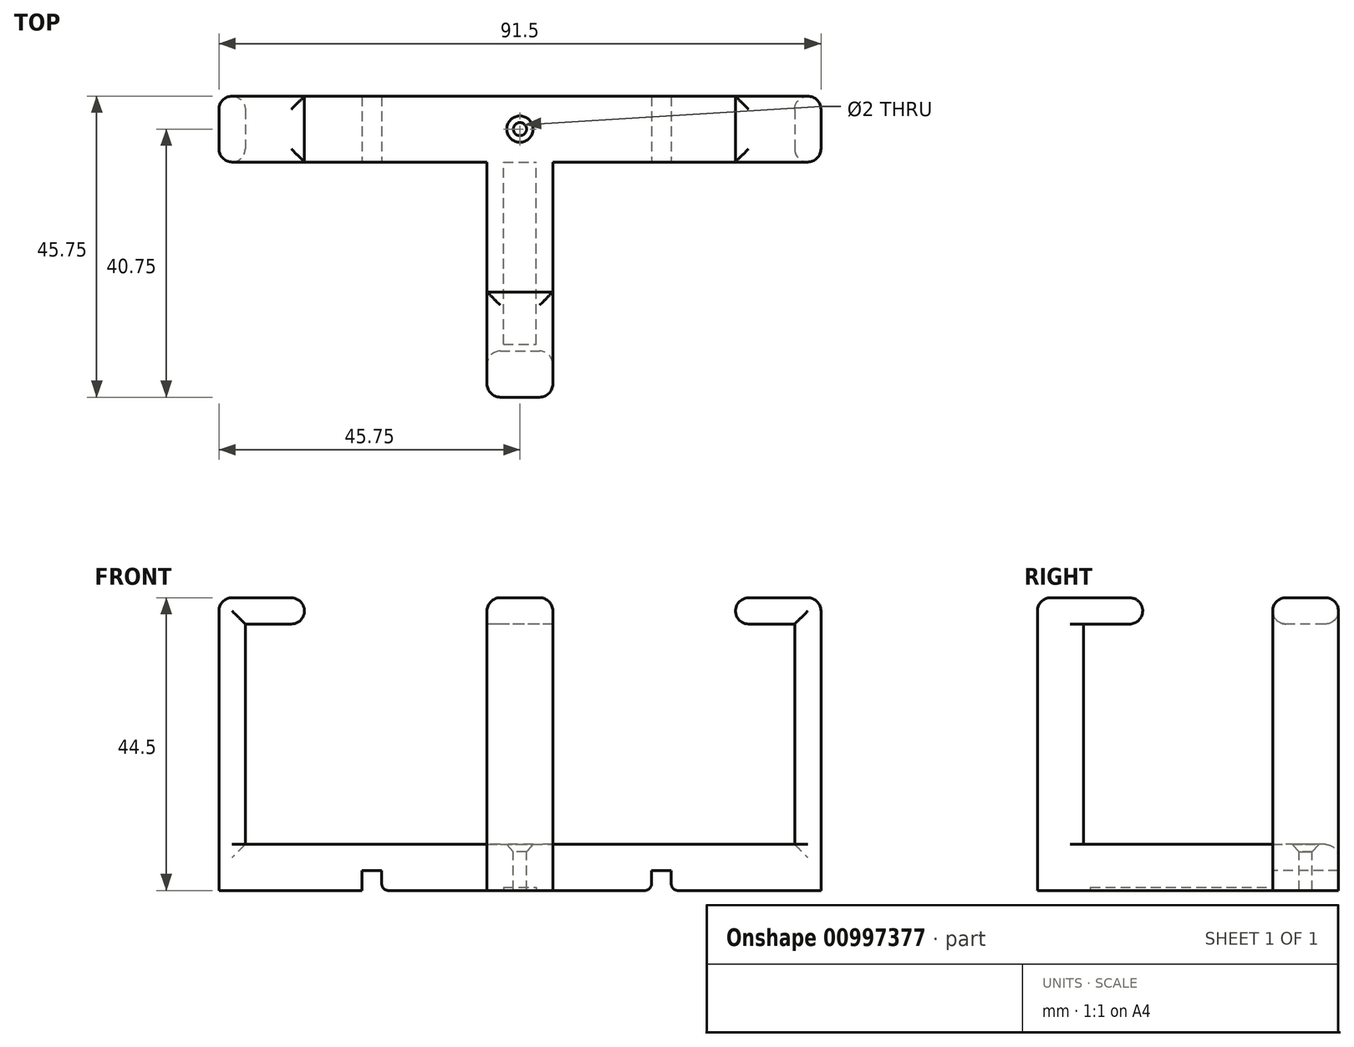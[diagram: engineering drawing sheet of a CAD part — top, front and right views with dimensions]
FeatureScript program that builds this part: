
annotation { "Feature Type Name" : "Feature", "Feature Type Description" : "" }
export const myFeature = defineFeature(function(context is Context, id is Id, definition is map)
    precondition{}
    {
        {
            var Q0;
            Q0=qCreatedBy(makeId("Front.planeOp"),FACE);
            var sketch = newSketch(context, id + "F0", { "sketchPlane" : qUnion([Q0])});
            skLineSegment(sketch, "E0.bottom", {"start": v(-45.75, -3.5) * mm, "end": v(45.75, -3.5) * mm});
            skLineSegment(sketch, "E0.top", {"start": v(-45.75, 3.5) * mm, "end": v(45.75, 3.5) * mm});
            skLineSegment(sketch, "E0.left", {"start": v(-45.75, -3.5) * mm, "end": v(-45.75, 3.5) * mm});
            skLineSegment(sketch, "E0.right", {"start": v(45.75, -3.5) * mm, "end": v(45.75, 3.5) * mm});
            skPoint(sketch, "E0.middle", {"position": v(0, 0) * mm});
            skSolve(sketch);
        }
        {
            var Q0;
            Q0 = qSketchRegion(id + "F0", true);
            extrude(context, id + "F1", {"entities" : qUnion([Q0]), "endBound" : BoundingType.SYMMETRIC, "depth" : 10 * mm, "offsetDistance" : 25 * mm});
        }
        {
            var Q0;
            Q0=qCreatedBy(makeId("Top.planeOp"),FACE);
            var sketch = newSketch(context, id + "F2", { "sketchPlane" : qUnion([Q0])});
            skLineSegment(sketch, "E1.bottom", {"start": v(0, 0) * mm, "end": v(-5, 0) * mm});
            skLineSegment(sketch, "E1.top", {"start": v(0, -40.75) * mm, "end": v(-5, -40.75) * mm});
            skLineSegment(sketch, "E1.left", {"start": v(0, 0) * mm, "end": v(0, -40.75) * mm});
            skLineSegment(sketch, "E1.right", {"start": v(-5, 0) * mm, "end": v(-5, -40.75) * mm});
            skPoint(sketch, "E2.oppositeSnap0", {"position": v(-2.5, -40.75) * mm});
            skLineSegment(sketch, "E2.bottom", {"start": v(0, 0) * mm, "end": v(5, 0) * mm});
            skLineSegment(sketch, "E2.top", {"start": v(0, -40.75) * mm, "end": v(5, -40.75) * mm});
            skLineSegment(sketch, "E2.right", {"start": v(5, 0) * mm, "end": v(5, -40.75) * mm});
            skSolve(sketch);
        }
        {
            var Q0;
            Q0 = qSketchRegion(id + "F2", true);
            extrude(context, id + "F3", {"entities" : qUnion([Q0]), "operationType" : NewBodyOperationType.ADD, "endBound" : BoundingType.SYMMETRIC, "depth" : 7 * mm, "offsetDistance" : 25 * mm});
        }
        {
            var Q0;
            Q0=makeQuery(id+"F3.boolean.opBoolean","MERGE",FACE,{"derivedFrom":[makeQuery(id+"F1.opExtrude","SWEPT_FACE",FACE,{"disambiguationData":[OSD([sQuery(id+"F0.wireOp",EDGE,"E0.top")])]}),makeQuery(id+"F3.opExtrude","CAP_FACE",FACE,{"disambiguationData":[OSD([sQuery(id+"F2.wireOp",EDGE,"E1.bottom"),sQuery(id+"F2.wireOp",EDGE,"E1.top"),sQuery(id+"F2.wireOp",EDGE,"E1.right"),sQuery(id+"F2.wireOp",EDGE,"E2.bottom"),sQuery(id+"F2.wireOp",EDGE,"E2.top"),sQuery(id+"F2.wireOp",EDGE,"E2.right")])],"isStart":false})]});
            var sketch = newSketch(context, id + "F4", { "sketchPlane" : qUnion([Q0])});
            skLineSegment(sketch, "E3.bottom", {"start": v(-45.75, 5) * mm, "end": v(-41.75, 5) * mm});
            skLineSegment(sketch, "E3.top", {"start": v(-45.75, -5) * mm, "end": v(-41.75, -5) * mm});
            skLineSegment(sketch, "E3.left", {"start": v(-45.75, 5) * mm, "end": v(-45.75, -5) * mm});
            skLineSegment(sketch, "E3.right", {"start": v(-41.75, 5) * mm, "end": v(-41.75, -5) * mm});
            skSolve(sketch);
        }
        {
            var Q0;
            Q0 = qSketchRegion(id + "F4", true);
            extrude(context, id + "F5", {"entities" : qUnion([Q0]), "operationType" : NewBodyOperationType.ADD, "depth" : 37.5 * mm, "offsetDistance" : 25 * mm});
        }
        {
            var Q0;
            Q0=makeQuery(id+"F3.boolean.opBoolean","MERGE",FACE,{"derivedFrom":[makeQuery(id+"F1.opExtrude","SWEPT_FACE",FACE,{"disambiguationData":[OSD([sQuery(id+"F0.wireOp",EDGE,"E0.top")])]}),makeQuery(id+"F3.opExtrude","CAP_FACE",FACE,{"disambiguationData":[OSD([sQuery(id+"F2.wireOp",EDGE,"E1.bottom"),sQuery(id+"F2.wireOp",EDGE,"E1.top"),sQuery(id+"F2.wireOp",EDGE,"E1.right"),sQuery(id+"F2.wireOp",EDGE,"E2.bottom"),sQuery(id+"F2.wireOp",EDGE,"E2.top"),sQuery(id+"F2.wireOp",EDGE,"E2.right")])],"isStart":false})]});
            var sketch = newSketch(context, id + "F6", { "sketchPlane" : qUnion([Q0])});
            skLineSegment(sketch, "E4.bottom", {"start": v(45.75, 5) * mm, "end": v(41.75, 5) * mm});
            skLineSegment(sketch, "E4.top", {"start": v(45.75, -5) * mm, "end": v(41.75, -5) * mm});
            skLineSegment(sketch, "E4.left", {"start": v(45.75, 5) * mm, "end": v(45.75, -5) * mm});
            skLineSegment(sketch, "E4.right", {"start": v(41.75, 5) * mm, "end": v(41.75, -5) * mm});
            skSolve(sketch);
        }
        {
            var Q0;
            Q0 = qSketchRegion(id + "F6", true);
            extrude(context, id + "F7", {"entities" : qUnion([Q0]), "operationType" : NewBodyOperationType.ADD, "depth" : 37.5 * mm, "offsetDistance" : 25 * mm});
        }
        {
            var Q0;
            Q0=makeQuery(id+"F3.boolean.opBoolean","MERGE",FACE,{"derivedFrom":[makeQuery(id+"F1.opExtrude","SWEPT_FACE",FACE,{"disambiguationData":[OSD([sQuery(id+"F0.wireOp",EDGE,"E0.top")])]}),makeQuery(id+"F3.opExtrude","CAP_FACE",FACE,{"disambiguationData":[OSD([sQuery(id+"F2.wireOp",EDGE,"E1.bottom"),sQuery(id+"F2.wireOp",EDGE,"E1.top"),sQuery(id+"F2.wireOp",EDGE,"E1.right"),sQuery(id+"F2.wireOp",EDGE,"E2.bottom"),sQuery(id+"F2.wireOp",EDGE,"E2.top"),sQuery(id+"F2.wireOp",EDGE,"E2.right")])],"isStart":false})]});
            var sketch = newSketch(context, id + "F8", { "sketchPlane" : qUnion([Q0])});
            skLineSegment(sketch, "E5.bottom", {"start": v(-5, -40.75) * mm, "end": v(5, -40.75) * mm});
            skLineSegment(sketch, "E5.top", {"start": v(-5, -33.75) * mm, "end": v(5, -33.75) * mm});
            skLineSegment(sketch, "E5.left", {"start": v(-5, -40.75) * mm, "end": v(-5, -33.75) * mm});
            skLineSegment(sketch, "E5.right", {"start": v(5, -40.75) * mm, "end": v(5, -33.75) * mm});
            skSolve(sketch);
        }
        {
            var Q0;
            Q0 = qSketchRegion(id + "F8", true);
            extrude(context, id + "F9", {"entities" : qUnion([Q0]), "operationType" : NewBodyOperationType.ADD, "depth" : 37.5 * mm, "offsetDistance" : 25 * mm});
        }
        {
            var Q0;
            Q0=makeQuery(id+"F9.opExtrude","SWEPT_FACE",FACE,{"disambiguationData":[OSD([sQuery(id+"F8.wireOp",EDGE,"E5.top")])]});
            var sketch = newSketch(context, id + "F10", { "sketchPlane" : qUnion([Q0])});
            skLineSegment(sketch, "E6.bottom", {"start": v(-5, 41) * mm, "end": v(5, 41) * mm});
            skLineSegment(sketch, "E6.top", {"start": v(-5, 37) * mm, "end": v(5, 37) * mm});
            skLineSegment(sketch, "E6.left", {"start": v(-5, 41) * mm, "end": v(-5, 37) * mm});
            skLineSegment(sketch, "E6.right", {"start": v(5, 41) * mm, "end": v(5, 37) * mm});
            skSolve(sketch);
        }
        {
            var Q0;
            Q0 = qSketchRegion(id + "F10", true);
            extrude(context, id + "F11", {"entities" : qUnion([Q0]), "operationType" : NewBodyOperationType.ADD, "depth" : 9 * mm, "offsetDistance" : 25 * mm});
        }
        {
            var Q0;
            Q0=makeQuery(id+"F7.opExtrude","SWEPT_FACE",FACE,{"disambiguationData":[OSD([sQuery(id+"F6.wireOp",EDGE,"E4.right")])]});
            var sketch = newSketch(context, id + "F12", { "sketchPlane" : qUnion([Q0])});
            skLineSegment(sketch, "E7.bottom", {"start": v(-5, 41) * mm, "end": v(5, 41) * mm});
            skLineSegment(sketch, "E7.top", {"start": v(-5, 37) * mm, "end": v(5, 37) * mm});
            skLineSegment(sketch, "E7.left", {"start": v(-5, 41) * mm, "end": v(-5, 37) * mm});
            skLineSegment(sketch, "E7.right", {"start": v(5, 41) * mm, "end": v(5, 37) * mm});
            skSolve(sketch);
        }
        {
            var Q0;
            Q0 = qSketchRegion(id + "F12", true);
            extrude(context, id + "F13", {"entities" : qUnion([Q0]), "operationType" : NewBodyOperationType.ADD, "depth" : 9 * mm, "offsetDistance" : 25 * mm});
        }
        {
            var Q0;
            Q0=makeQuery(id+"F5.opExtrude","SWEPT_FACE",FACE,{"disambiguationData":[OSD([sQuery(id+"F4.wireOp",EDGE,"E3.right")])]});
            var sketch = newSketch(context, id + "F14", { "sketchPlane" : qUnion([Q0])});
            skLineSegment(sketch, "E8.bottom", {"start": v(-5, 41) * mm, "end": v(5, 41) * mm});
            skLineSegment(sketch, "E8.top", {"start": v(-5, 37) * mm, "end": v(5, 37) * mm});
            skLineSegment(sketch, "E8.left", {"start": v(-5, 41) * mm, "end": v(-5, 37) * mm});
            skLineSegment(sketch, "E8.right", {"start": v(5, 41) * mm, "end": v(5, 37) * mm});
            skSolve(sketch);
        }
        {
            var Q0;
            Q0 = qSketchRegion(id + "F14", true);
            extrude(context, id + "F15", {"entities" : qUnion([Q0]), "operationType" : NewBodyOperationType.ADD, "depth" : 9 * mm, "offsetDistance" : 25 * mm});
        }
        {
            var Q0;
            Q0=makeQuery(id+"F1.opExtrude","CAP_EDGE",EDGE,{"disambiguationData":[OSD([sQuery(id+"F0.wireOp",EDGE,"E0.top")])],"isStart":true});
            var Q1;
            Q1=makeQuery(id+"F7.opExtrude","SWEPT_EDGE",EDGE,{"disambiguationData":[OSD([sQuery(id+"F0.wireOp",EDGE,"E0.top"),sQuery(id+"F6.wireOp",EDGE,"E4.bottom"),sQuery(id+"F6.wireOp",EDGE,"E4.right")])]});
            var Q2;
            Q2=makeQuery(id+"F13.opExtrude","SWEPT_EDGE",EDGE,{"disambiguationData":[OSD([sQuery(id+"F0.wireOp",EDGE,"E0.top"),sQuery(id+"F6.wireOp",EDGE,"E4.bottom"),sQuery(id+"F6.wireOp",EDGE,"E4.right"),sQuery(id+"F12.wireOp",EDGE,"E7.top"),sQuery(id+"F12.wireOp",EDGE,"E7.left")])]});
            var Q3;
            Q3=makeQuery(id+"F5.opExtrude","SWEPT_EDGE",EDGE,{"disambiguationData":[OSD([sQuery(id+"F0.wireOp",EDGE,"E0.top"),sQuery(id+"F4.wireOp",EDGE,"E3.bottom"),sQuery(id+"F4.wireOp",EDGE,"E3.right")])]});
            var Q4;
            Q4=makeQuery(id+"F15.opExtrude","SWEPT_EDGE",EDGE,{"disambiguationData":[OSD([sQuery(id+"F0.wireOp",EDGE,"E0.top"),sQuery(id+"F4.wireOp",EDGE,"E3.bottom"),sQuery(id+"F4.wireOp",EDGE,"E3.right"),sQuery(id+"F14.wireOp",EDGE,"E8.top"),sQuery(id+"F14.wireOp",EDGE,"E8.right")])]});
            var Q5;
            Q5=makeQuery(id+"F13.opExtrude","CAP_EDGE",EDGE,{"disambiguationData":[OSD([sQuery(id+"F12.wireOp",EDGE,"E7.bottom")])],"isStart":false});
            var Q6;
            Q6=makeQuery(id+"F13.boolean.opBoolean","MERGE",EDGE,{"derivedFrom":[makeQuery(id+"F7.opExtrude","CAP_EDGE",EDGE,{"disambiguationData":[OSD([sQuery(id+"F6.wireOp",EDGE,"E4.bottom")])],"isStart":false}),makeQuery(id+"F13.opExtrude","SWEPT_EDGE",EDGE,{"disambiguationData":[OSD([sQuery(id+"F12.wireOp",EDGE,"E7.bottom"),sQuery(id+"F12.wireOp",EDGE,"E7.left")])]})]});
            var Q7;
            Q7=makeQuery(id+"F7.boolean.opBoolean","MERGE",EDGE,{"derivedFrom":[makeQuery(id+"F1.opExtrude","CAP_EDGE",EDGE,{"disambiguationData":[OSD([sQuery(id+"F0.wireOp",EDGE,"E0.right")])],"isStart":true}),makeQuery(id+"F7.opExtrude","SWEPT_EDGE",EDGE,{"disambiguationData":[OSD([sQuery(id+"F6.wireOp",EDGE,"E4.bottom"),sQuery(id+"F6.wireOp",EDGE,"E4.left")])]})]});
            var Q8;
            Q8=makeQuery(id+"F5.boolean.opBoolean","MERGE",EDGE,{"derivedFrom":[makeQuery(id+"F1.opExtrude","CAP_EDGE",EDGE,{"disambiguationData":[OSD([sQuery(id+"F0.wireOp",EDGE,"E0.left")])],"isStart":true}),makeQuery(id+"F5.opExtrude","SWEPT_EDGE",EDGE,{"disambiguationData":[OSD([sQuery(id+"F4.wireOp",EDGE,"E3.bottom"),sQuery(id+"F4.wireOp",EDGE,"E3.left")])]})]});
            var Q9;
            Q9=makeQuery(id+"F15.boolean.opBoolean","MERGE",EDGE,{"derivedFrom":[makeQuery(id+"F5.opExtrude","CAP_EDGE",EDGE,{"disambiguationData":[OSD([sQuery(id+"F4.wireOp",EDGE,"E3.bottom")])],"isStart":false}),makeQuery(id+"F15.opExtrude","SWEPT_EDGE",EDGE,{"disambiguationData":[OSD([sQuery(id+"F14.wireOp",EDGE,"E8.bottom"),sQuery(id+"F14.wireOp",EDGE,"E8.right")])]})]});
            var Q10;
            Q10=makeQuery(id+"F15.opExtrude","CAP_EDGE",EDGE,{"disambiguationData":[OSD([sQuery(id+"F14.wireOp",EDGE,"E8.bottom")])],"isStart":false});
            var Q11;
            Q11=makeQuery(id+"F11.opExtrude","CAP_EDGE",EDGE,{"disambiguationData":[OSD([sQuery(id+"F10.wireOp",EDGE,"E6.bottom")])],"isStart":false});
            var Q12;
            Q12=makeQuery(id+"F9.opExtrude","SWEPT_EDGE",EDGE,{"disambiguationData":[OSD([sQuery(id+"F2.wireOp",EDGE,"E1.right"),sQuery(id+"F8.wireOp",EDGE,"E5.top"),sQuery(id+"F8.wireOp",EDGE,"E5.left")])]});
            var Q13;
            Q13=makeQuery(id+"F9.opExtrude","SWEPT_EDGE",EDGE,{"disambiguationData":[OSD([sQuery(id+"F2.wireOp",EDGE,"E2.right"),sQuery(id+"F8.wireOp",EDGE,"E5.top"),sQuery(id+"F8.wireOp",EDGE,"E5.right")])]});
            var Q14;
            Q14=makeQuery(id+"F5.opExtrude","SWEPT_EDGE",EDGE,{"disambiguationData":[OSD([sQuery(id+"F0.wireOp",EDGE,"E0.top"),sQuery(id+"F4.wireOp",EDGE,"E3.top"),sQuery(id+"F4.wireOp",EDGE,"E3.right")])]});
            var Q15;
            Q15=makeQuery(id+"F7.opExtrude","SWEPT_EDGE",EDGE,{"disambiguationData":[OSD([sQuery(id+"F0.wireOp",EDGE,"E0.top"),sQuery(id+"F6.wireOp",EDGE,"E4.top"),sQuery(id+"F6.wireOp",EDGE,"E4.right")])]});
            var Q16;
            Q16=makeQuery(id+"F15.opExtrude","SWEPT_EDGE",EDGE,{"disambiguationData":[OSD([sQuery(id+"F0.wireOp",EDGE,"E0.top"),sQuery(id+"F4.wireOp",EDGE,"E3.top"),sQuery(id+"F4.wireOp",EDGE,"E3.right"),sQuery(id+"F14.wireOp",EDGE,"E8.top"),sQuery(id+"F14.wireOp",EDGE,"E8.left")])]});
            var Q17;
            Q17=makeQuery(id+"F13.opExtrude","SWEPT_EDGE",EDGE,{"disambiguationData":[OSD([sQuery(id+"F0.wireOp",EDGE,"E0.top"),sQuery(id+"F6.wireOp",EDGE,"E4.top"),sQuery(id+"F6.wireOp",EDGE,"E4.right"),sQuery(id+"F12.wireOp",EDGE,"E7.top"),sQuery(id+"F12.wireOp",EDGE,"E7.right")])]});
            var Q18;
            Q18=makeQuery(id+"F5.opExtrude","CAP_EDGE",EDGE,{"disambiguationData":[OSD([sQuery(id+"F4.wireOp",EDGE,"E3.left")])],"isStart":false});
            var Q19;
            Q19=makeQuery(id+"F7.opExtrude","CAP_EDGE",EDGE,{"disambiguationData":[OSD([sQuery(id+"F6.wireOp",EDGE,"E4.left")])],"isStart":false});
            var Q20;
            Q20=makeQuery(id+"F9.opExtrude","CAP_EDGE",EDGE,{"disambiguationData":[OSD([sQuery(id+"F8.wireOp",EDGE,"E5.bottom")])],"isStart":false});
            var Q21;
            Q21=makeQuery(id+"F11.boolean.opBoolean","MERGE",EDGE,{"derivedFrom":[makeQuery(id+"F9.opExtrude","CAP_EDGE",EDGE,{"disambiguationData":[OSD([sQuery(id+"F8.wireOp",EDGE,"E5.right")])],"isStart":false}),makeQuery(id+"F11.opExtrude","SWEPT_EDGE",EDGE,{"disambiguationData":[OSD([sQuery(id+"F10.wireOp",EDGE,"E6.bottom"),sQuery(id+"F10.wireOp",EDGE,"E6.left")])]})]});
            var Q22;
            Q22=makeQuery(id+"F11.boolean.opBoolean","MERGE",EDGE,{"derivedFrom":[makeQuery(id+"F9.opExtrude","CAP_EDGE",EDGE,{"disambiguationData":[OSD([sQuery(id+"F8.wireOp",EDGE,"E5.left")])],"isStart":false}),makeQuery(id+"F11.opExtrude","SWEPT_EDGE",EDGE,{"disambiguationData":[OSD([sQuery(id+"F10.wireOp",EDGE,"E6.bottom"),sQuery(id+"F10.wireOp",EDGE,"E6.right")])]})]});
            var Q23;
            Q23=makeQuery(id+"F11.opExtrude","CAP_EDGE",EDGE,{"disambiguationData":[OSD([sQuery(id+"F10.wireOp",EDGE,"E6.top")])],"isStart":false});
            var Q24;
            Q24=makeQuery(id+"F9.boolean.opBoolean","MERGE",EDGE,{"derivedFrom":[makeQuery(id+"F3.opExtrude","SWEPT_EDGE",EDGE,{"disambiguationData":[OSD([sQuery(id+"F2.wireOp",EDGE,"E1.top"),sQuery(id+"F2.wireOp",EDGE,"E1.right")])]}),makeQuery(id+"F9.opExtrude","SWEPT_EDGE",EDGE,{"disambiguationData":[OSD([sQuery(id+"F8.wireOp",EDGE,"E5.bottom"),sQuery(id+"F8.wireOp",EDGE,"E5.left")])]})]});
            var Q25;
            Q25=makeQuery(id+"F9.boolean.opBoolean","MERGE",EDGE,{"derivedFrom":[makeQuery(id+"F3.opExtrude","SWEPT_EDGE",EDGE,{"disambiguationData":[OSD([sQuery(id+"F2.wireOp",EDGE,"E2.top"),sQuery(id+"F2.wireOp",EDGE,"E2.right")])]}),makeQuery(id+"F9.opExtrude","SWEPT_EDGE",EDGE,{"disambiguationData":[OSD([sQuery(id+"F8.wireOp",EDGE,"E5.bottom"),sQuery(id+"F8.wireOp",EDGE,"E5.right")])]})]});
            var Q26;
            Q26=makeQuery(id+"F13.boolean.opBoolean","MERGE",EDGE,{"derivedFrom":[makeQuery(id+"F7.opExtrude","CAP_EDGE",EDGE,{"disambiguationData":[OSD([sQuery(id+"F6.wireOp",EDGE,"E4.top")])],"isStart":false}),makeQuery(id+"F13.opExtrude","SWEPT_EDGE",EDGE,{"disambiguationData":[OSD([sQuery(id+"F12.wireOp",EDGE,"E7.bottom"),sQuery(id+"F12.wireOp",EDGE,"E7.right")])]})]});
            var Q27;
            Q27=makeQuery(id+"F15.boolean.opBoolean","MERGE",EDGE,{"derivedFrom":[makeQuery(id+"F5.opExtrude","CAP_EDGE",EDGE,{"disambiguationData":[OSD([sQuery(id+"F4.wireOp",EDGE,"E3.top")])],"isStart":false}),makeQuery(id+"F15.opExtrude","SWEPT_EDGE",EDGE,{"disambiguationData":[OSD([sQuery(id+"F14.wireOp",EDGE,"E8.bottom"),sQuery(id+"F14.wireOp",EDGE,"E8.left")])]})]});
            var Q28;
            Q28=makeQuery(id+"F5.boolean.opBoolean","MERGE",EDGE,{"derivedFrom":[makeQuery(id+"F1.opExtrude","CAP_EDGE",EDGE,{"disambiguationData":[OSD([sQuery(id+"F0.wireOp",EDGE,"E0.left")])],"isStart":false}),makeQuery(id+"F5.opExtrude","SWEPT_EDGE",EDGE,{"disambiguationData":[OSD([sQuery(id+"F4.wireOp",EDGE,"E3.top"),sQuery(id+"F4.wireOp",EDGE,"E3.left")])]})]});
            var Q29;
            Q29=makeQuery(id+"F7.boolean.opBoolean","MERGE",EDGE,{"derivedFrom":[makeQuery(id+"F1.opExtrude","CAP_EDGE",EDGE,{"disambiguationData":[OSD([sQuery(id+"F0.wireOp",EDGE,"E0.right")])],"isStart":false}),makeQuery(id+"F7.opExtrude","SWEPT_EDGE",EDGE,{"disambiguationData":[OSD([sQuery(id+"F6.wireOp",EDGE,"E4.top"),sQuery(id+"F6.wireOp",EDGE,"E4.left")])]})]});
            var Q30;
            Q30=makeQuery(id+"F15.opExtrude","CAP_EDGE",EDGE,{"disambiguationData":[OSD([sQuery(id+"F14.wireOp",EDGE,"E8.top")])],"isStart":false});
            var Q31;
            Q31=makeQuery(id+"F13.opExtrude","CAP_EDGE",EDGE,{"disambiguationData":[OSD([sQuery(id+"F12.wireOp",EDGE,"E7.top")])],"isStart":false});
            fillet(context, id + "F16", {"entities" : qUnion([Q0, Q1, Q2, Q3, Q4, Q5, Q6, Q7, Q8, Q9, Q10, Q11, Q12, Q13, Q14, Q15, Q16, Q17, Q18, Q19, Q20, Q21, Q22, Q23, Q24, Q25, Q26, Q27, Q28, Q29, Q30, Q31]), "radius" : 2 * mm, "tangentPropagation" : true, "allowEdgeOverflow" : false});
        }
        {
            var Q0;
            Q0=makeQuery(id+"F3.boolean.opBoolean","MERGE",FACE,{"derivedFrom":[makeQuery(id+"F1.opExtrude","SWEPT_FACE",FACE,{"disambiguationData":[OSD([sQuery(id+"F0.wireOp",EDGE,"E0.top")])]}),makeQuery(id+"F3.opExtrude","CAP_FACE",FACE,{"disambiguationData":[OSD([sQuery(id+"F2.wireOp",EDGE,"E1.bottom"),sQuery(id+"F2.wireOp",EDGE,"E1.top"),sQuery(id+"F2.wireOp",EDGE,"E1.right"),sQuery(id+"F2.wireOp",EDGE,"E2.bottom"),sQuery(id+"F2.wireOp",EDGE,"E2.top"),sQuery(id+"F2.wireOp",EDGE,"E2.right")])],"isStart":false})]});
            var sketch = newSketch(context, id + "F17", { "sketchPlane" : qUnion([Q0])});
            skCircle(sketch, "E9", {"center": v(0, 0) * mm, "radius": 2 * mm});
            skSolve(sketch);
        }
        {
            var Q0;
            Q0=sQuery(id+"F17.wireOp",VERTEX,"E9.center");
            var Q1;
            Q1=makeQuery(id+"F1.opExtrude","SWEPT_BODY",BODY,{"disambiguationData":[OSD([sQuery(id+"F0.wireOp",EDGE,"E0.bottom"),sQuery(id+"F0.wireOp",EDGE,"E0.top"),sQuery(id+"F0.wireOp",EDGE,"E0.left"),sQuery(id+"F0.wireOp",EDGE,"E0.right")])]});
            hole(context, id + "F18", {"style" : HoleStyle.C_SINK, "endStyle" : HoleEndStyle.BLIND, "holeDiameter" : 2 * mm, "cSinkDiameter" : 4 * mm, "cSinkAngle" : 82 * degree, "majorDiameter" : 5 * mm, "holeDepth" : 18 * mm, "isTappedThrough" : true, "tappedDepth" : 12 * mm, "tapClearance" : 3, "startFromSketch" : true, "locations" : qUnion([Q0]), "scope" : qUnion([Q1])});
        }
        {
            var Q0;
            Q0=makeQuery(id+"F3.boolean.opBoolean","MERGE",FACE,{"derivedFrom":[makeQuery(id+"F1.opExtrude","SWEPT_FACE",FACE,{"disambiguationData":[OSD([sQuery(id+"F0.wireOp",EDGE,"E0.bottom")])]}),makeQuery(id+"F3.opExtrude","CAP_FACE",FACE,{"disambiguationData":[OSD([sQuery(id+"F2.wireOp",EDGE,"E1.bottom"),sQuery(id+"F2.wireOp",EDGE,"E1.top"),sQuery(id+"F2.wireOp",EDGE,"E1.right"),sQuery(id+"F2.wireOp",EDGE,"E2.bottom"),sQuery(id+"F2.wireOp",EDGE,"E2.top"),sQuery(id+"F2.wireOp",EDGE,"E2.right")])],"isStart":true})]});
            var sketch = newSketch(context, id + "F19", { "sketchPlane" : qUnion([Q0])});
            skLineSegment(sketch, "E10.bottom", {"start": v(20, -5) * mm, "end": v(23, -5) * mm});
            skLineSegment(sketch, "E10.top", {"start": v(20, 5) * mm, "end": v(23, 5) * mm});
            skLineSegment(sketch, "E10.left", {"start": v(20, -5) * mm, "end": v(20, 5) * mm});
            skLineSegment(sketch, "E10.right", {"start": v(23, -5) * mm, "end": v(23, 5) * mm});
            skLineSegment(sketch, "E11.bottom", {"start": v(-21, -5) * mm, "end": v(-24, -5) * mm});
            skLineSegment(sketch, "E11.top", {"start": v(-21, 5) * mm, "end": v(-24, 5) * mm});
            skLineSegment(sketch, "E11.left", {"start": v(-21, -5) * mm, "end": v(-21, 5) * mm});
            skLineSegment(sketch, "E11.right", {"start": v(-24, -5) * mm, "end": v(-24, 5) * mm});
            skSolve(sketch);
        }
        {
            var Q0;
            Q0 = qSketchRegion(id + "F19", true);
            extrude(context, id + "F20", {"entities" : qUnion([Q0]), "operationType" : NewBodyOperationType.REMOVE, "oppositeDirection" : true, "depth" : 3 * mm, "offsetDistance" : 25 * mm});
        }
        {
            var Q0;
            Q0=makeQuery(id+"F20.boolean.opBoolean","COPY",EDGE,{"derivedFrom":makeQuery(id+"F20.opExtrude","CAP_EDGE",EDGE,{"disambiguationData":[OSD([sQuery(id+"F19.wireOp",EDGE,"E10.left")])],"isStart":true})});
            var Q1;
            Q1=makeQuery(id+"F20.boolean.opBoolean","COPY",EDGE,{"derivedFrom":makeQuery(id+"F20.opExtrude","CAP_EDGE",EDGE,{"disambiguationData":[OSD([sQuery(id+"F19.wireOp",EDGE,"E10.right")])],"isStart":true})});
            var Q2;
            Q2=makeQuery(id+"F20.boolean.opBoolean","COPY",EDGE,{"derivedFrom":makeQuery(id+"F20.opExtrude","CAP_EDGE",EDGE,{"disambiguationData":[OSD([sQuery(id+"F19.wireOp",EDGE,"E11.left")])],"isStart":true})});
            var Q3;
            Q3=makeQuery(id+"F20.boolean.opBoolean","COPY",EDGE,{"derivedFrom":makeQuery(id+"F20.opExtrude","CAP_EDGE",EDGE,{"disambiguationData":[OSD([sQuery(id+"F19.wireOp",EDGE,"E11.right")])],"isStart":true})});
            fillet(context, id + "F21", {"entities" : qUnion([Q0, Q1, Q2, Q3]), "radius" : 1 * mm, "tangentPropagation" : true, "allowEdgeOverflow" : false});
        }
        {
            var Q0;
            {var subQ2=sQuery(id+"F2.wireOp",EDGE,"E2.right");var subQ3=sQuery(id+"F2.wireOp",EDGE,"E2.top");var subQ5=sQuery(id+"F2.wireOp",EDGE,"E1.right");var subQ6=sQuery(id+"F2.wireOp",EDGE,"E1.top");var subQ10=sQuery(id+"F0.wireOp",EDGE,"E0.bottom");Q0=makeQuery(id+"F20.boolean.opBoolean","SPLIT",FACE,{"disambiguationData":[TD([makeQuery(id+"F3.opExtrude","SWEPT_FACE",FACE,{"disambiguationData":[OSD([subQ5])]})])],"derivedFrom":makeQuery(id+"F3.boolean.opBoolean","MERGE",FACE,{"derivedFrom":[makeQuery(id+"F1.opExtrude","SWEPT_FACE",FACE,{"disambiguationData":[OSD([subQ10])]}),makeQuery(id+"F3.opExtrude","CAP_FACE",FACE,{"disambiguationData":[OSD([sQuery(id+"F2.wireOp",EDGE,"E1.bottom"),subQ6,subQ5,sQuery(id+"F2.wireOp",EDGE,"E2.bottom"),subQ3,subQ2])],"isStart":true})]})});}
            var sketch = newSketch(context, id + "F22", { "sketchPlane" : qUnion([Q0])});
            skLineSegment(sketch, "E12.bottom", {"start": v(-2.5, 32.7) * mm, "end": v(2.5, 32.7) * mm});
            skLineSegment(sketch, "E12.top", {"start": v(-2.5, 5) * mm, "end": v(2.5, 5) * mm});
            skLineSegment(sketch, "E12.left", {"start": v(-2.5, 32.7) * mm, "end": v(-2.5, 5) * mm});
            skLineSegment(sketch, "E12.right", {"start": v(2.5, 32.7) * mm, "end": v(2.5, 5) * mm});
            skPoint(sketch, "E12.middle", {"position": v(0, 18.85) * mm});
            skSolve(sketch);
        }
        {
            var Q0;
            Q0 = qSketchRegion(id + "F22", true);
            extrude(context, id + "F23", {"entities" : qUnion([Q0]), "operationType" : NewBodyOperationType.REMOVE, "oppositeDirection" : true, "depth" : .5 * mm, "offsetDistance" : 25 * mm});
        }
    });
